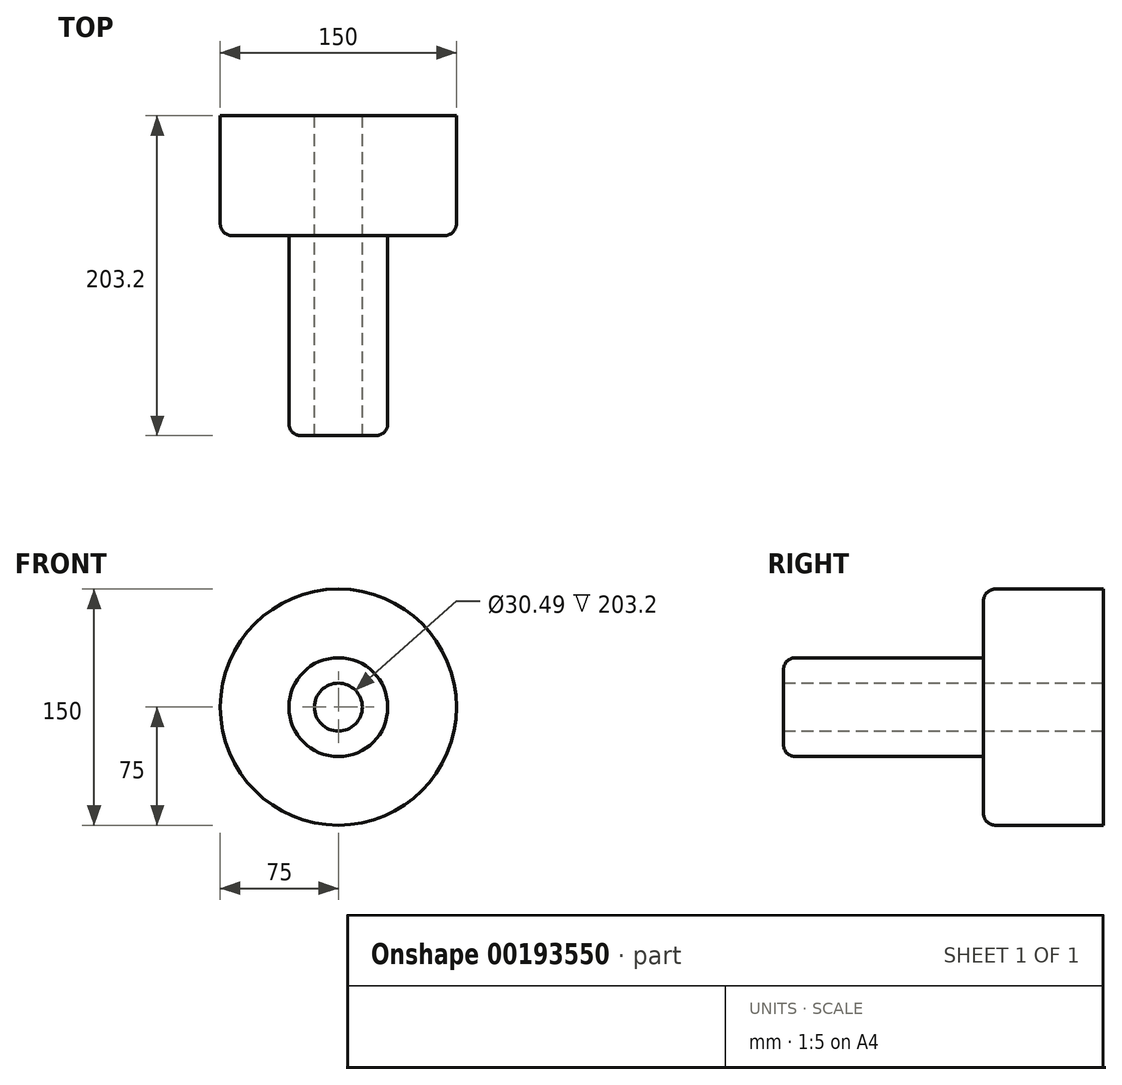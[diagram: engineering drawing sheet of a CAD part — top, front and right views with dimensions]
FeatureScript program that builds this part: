
annotation { "Feature Type Name" : "Feature", "Feature Type Description" : "" }
export const myFeature = defineFeature(function(context is Context, id is Id, definition is map)
    precondition{}
    {
        {
            var Q0;
            Q0=qCreatedBy(makeId("Front.planeOp"),FACE);
            var sketch = newSketch(context, id + "F0", { "sketchPlane" : qUnion([Q0])});
            skCircle(sketch, "E0", {"center": v(0, 0) * mm, "radius": 75 * mm});
            skSolve(sketch);
        }
        {
            var Q0;
            Q0=makeQuery(id+"F0.imprint","IMPRINT",FACE,{"disambiguationData":[TD([[makeQuery(id+"F0.imprint","IMPRINT",EDGE,{"derivedFrom":sQuery(id+"F0.wireOp",EDGE,"E0")}),1.0]])]});
            extrude(context, id + "F1", {"entities" : qUnion([Q0]), "depth" : 76.2 * mm});
        }
        {
            var Q0;
            Q0=makeQuery(id+"F1.opExtrude","CAP_FACE",FACE,{"disambiguationData":[OSD([sQuery(id+"F0.wireOp",EDGE,"E0")])],"isStart":false});
            var sketch = newSketch(context, id + "F2", { "sketchPlane" : qUnion([Q0])});
            skCircle(sketch, "E1", {"center": v(0, 0) * mm, "radius": 31.4 * mm});
            skSolve(sketch);
        }
        {
            var Q0;
            Q0=makeQuery(id+"F2.imprint","IMPRINT",FACE,{"disambiguationData":[TD([[makeQuery(id+"F2.imprint","IMPRINT",EDGE,{"derivedFrom":sQuery(id+"F2.wireOp",EDGE,"E1")}),1.0]])]});
            extrude(context, id + "F3", {"entities" : qUnion([Q0]), "operationType" : NewBodyOperationType.ADD, "depth" : 127 * mm});
        }
        {
            var Q0;
            Q0=qCreatedBy(makeId("Front.planeOp"),FACE);
            var sketch = newSketch(context, id + "F4", { "sketchPlane" : qUnion([Q0])});
            skCircle(sketch, "E2", {"center": v(0, 0) * mm, "radius": 15.25 * mm});
            skSolve(sketch);
        }
        {
            var Q0;
            Q0=makeQuery(id+"F3.opExtrude","CAP_FACE",FACE,{"disambiguationData":[OSD([sQuery(id+"F2.wireOp",EDGE,"E1")])],"isStart":false});
            var Q1;
            Q1=makeQuery(id+"F4.imprint","IMPRINT",FACE,{"disambiguationData":[TD([[makeQuery(id+"F4.imprint","IMPRINT",EDGE,{"derivedFrom":sQuery(id+"F4.wireOp",EDGE,"E2")}),1.0]])]});
            extrude(context, id + "F5", {"entities" : qUnion([Q0, Q1]), "operationType" : NewBodyOperationType.REMOVE, "depth" : 331.98 * mm});
        }
        {
            var Q0;
            Q0=makeQuery(id+"F3.opExtrude","CAP_EDGE",EDGE,{"disambiguationData":[OSD([sQuery(id+"F2.wireOp",EDGE,"E1")])],"isStart":false});
            fillet(context, id + "F6", {"entities" : qUnion([Q0]), "radius" : 7.62 * mm, "tangentPropagation" : true, "allowEdgeOverflow" : false});
        }
        {
            var Q0;
            Q0=makeQuery(id+"F1.opExtrude","CAP_EDGE",EDGE,{"disambiguationData":[OSD([sQuery(id+"F0.wireOp",EDGE,"E0")])],"isStart":false});
            fillet(context, id + "F7", {"entities" : qUnion([Q0]), "radius" : 7.62 * mm, "tangentPropagation" : true, "allowEdgeOverflow" : false});
        }
    });
